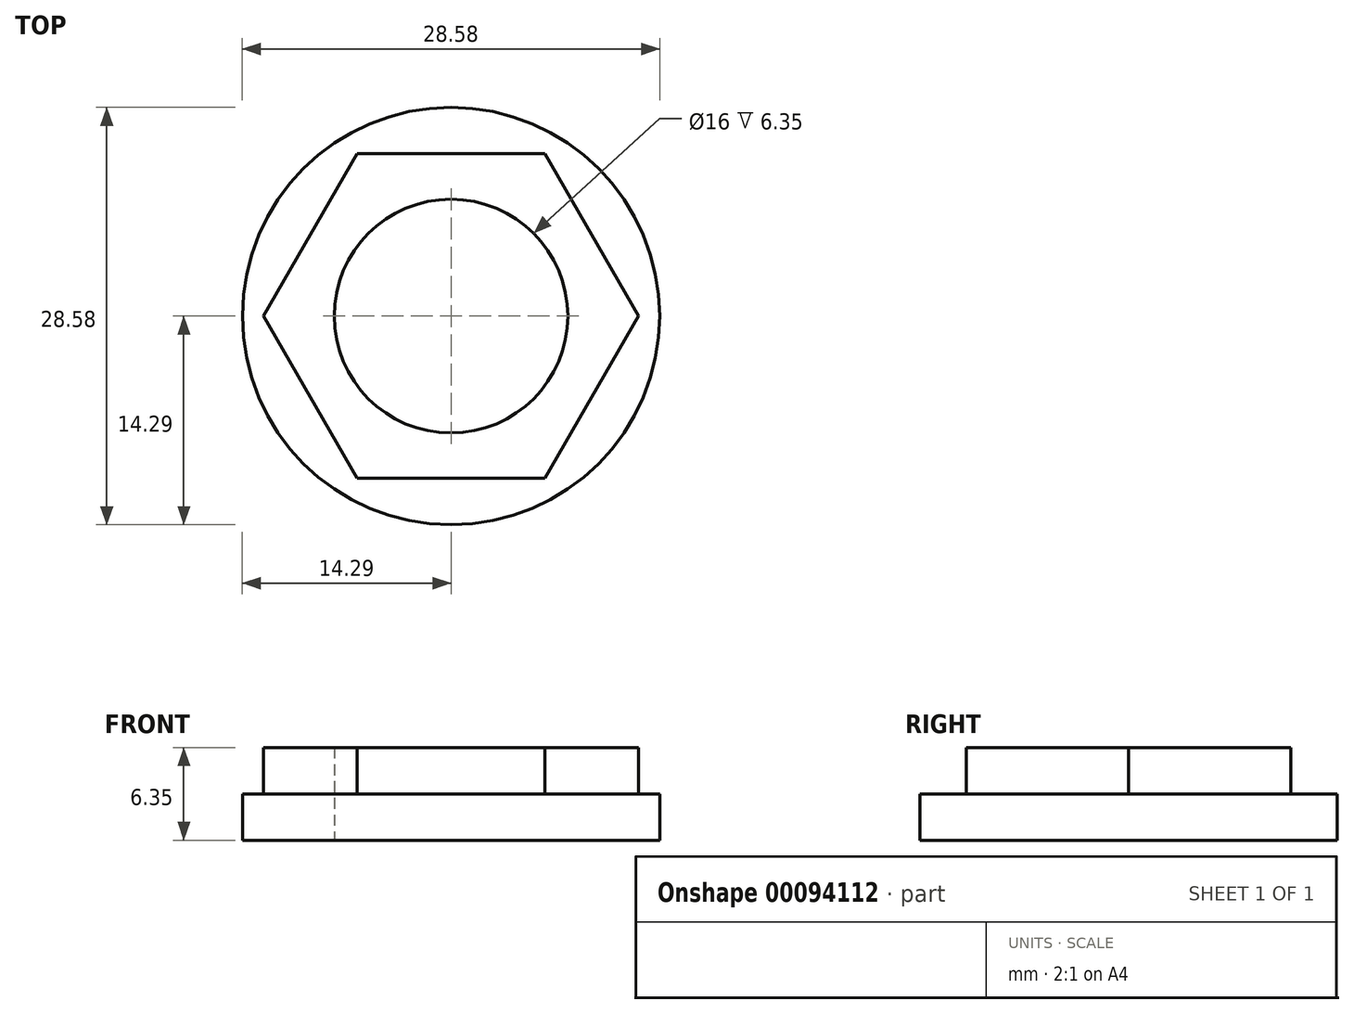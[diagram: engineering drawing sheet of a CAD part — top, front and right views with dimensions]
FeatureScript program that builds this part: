
annotation { "Feature Type Name" : "Feature", "Feature Type Description" : "" }
export const myFeature = defineFeature(function(context is Context, id is Id, definition is map)
    precondition{}
    {
        {
            var Q0;
            Q0=qCreatedBy(makeId("Top.planeOp"),FACE);
            var sketch = newSketch(context, id + "F0", { "sketchPlane" : qUnion([Q0])});
            skCircle(sketch, "E0", {"center": v(0, 0) * mm, "radius": 14.29 * mm});
            skSolve(sketch);
        }
        {
            var Q0;
            Q0=makeQuery(id+"F0.imprint","IMPRINT",FACE,{"disambiguationData":[TD([[makeQuery(id+"F0.imprint","IMPRINT",EDGE,{"derivedFrom":sQuery(id+"F0.wireOp",EDGE,"E0")}),1.0]])]});
            extrude(context, id + "F1", {"entities" : qUnion([Q0]), "depth" : 3.17 * mm});
        }
        {
            var Q0;
            Q0=makeQuery(id+"F1.opExtrude","CAP_FACE",FACE,{"disambiguationData":[OSD([sQuery(id+"F0.wireOp",EDGE,"E0")])],"isStart":false});
            var sketch = newSketch(context, id + "F2", { "sketchPlane" : qUnion([Q0])});
            skCircle(sketch, "E1.0", {"center": v(0, 0) * mm, "radius": 14.29 * mm});
            skCircle(sketch, "E2.cCircle", {"center": v(0, 0) * mm, "radius": 11.11 * mm, "construction": true});
            skLineSegment(sketch, "E2.0", {"start": v(-6.42, 11.11) * mm, "end": v(6.42, 11.11) * mm});
            skLineSegment(sketch, "E2.1", {"start": v(6.42, 11.11) * mm, "end": v(12.83, 0) * mm});
            skLineSegment(sketch, "E2.2", {"start": v(12.83, 0) * mm, "end": v(6.42, -11.11) * mm});
            skLineSegment(sketch, "E2.3", {"start": v(6.42, -11.11) * mm, "end": v(-6.42, -11.11) * mm});
            skLineSegment(sketch, "E2.4", {"start": v(-6.42, -11.11) * mm, "end": v(-12.83, 0) * mm});
            skLineSegment(sketch, "E2.5", {"start": v(-12.83, 0) * mm, "end": v(-6.42, 11.11) * mm});
            skPoint(sketch, "E2.0.midPoint", {"position": v(0, 11.11) * mm});
            skSolve(sketch);
        }
        {
            var Q0;
            Q0=makeQuery(id+"F2.imprint","IMPRINT",FACE,{"disambiguationData":[TD([[makeQuery(id+"F2.imprint","IMPRINT",EDGE,{"derivedFrom":sQuery(id+"F2.wireOp",EDGE,"E2.0")}),-1.0]])]});
            extrude(context, id + "F3", {"entities" : qUnion([Q0]), "operationType" : NewBodyOperationType.ADD, "depth" : 3.17 * mm});
        }
        {
            var Q0;
            Q0=makeQuery(id+"F1.opExtrude","CAP_FACE",FACE,{"disambiguationData":[OSD([sQuery(id+"F0.wireOp",EDGE,"E0")])],"isStart":true});
            var sketch = newSketch(context, id + "F4", { "sketchPlane" : qUnion([Q0])});
            skCircle(sketch, "E3.0", {"center": v(0, 0) * mm, "radius": 14.29 * mm});
            skCircle(sketch, "E4", {"center": v(0, 0) * mm, "radius": 8 * mm});
            skSolve(sketch);
        }
        {
            var Q0;
            Q0=makeQuery(id+"F4.imprint","IMPRINT",FACE,{"disambiguationData":[TD([[makeQuery(id+"F4.imprint","IMPRINT",EDGE,{"derivedFrom":sQuery(id+"F4.wireOp",EDGE,"E4")}),1.0]])]});
            extrude(context, id + "F5", {"entities" : qUnion([Q0]), "operationType" : NewBodyOperationType.REMOVE, "oppositeDirection" : true, "depth" : 25.4 * mm});
        }
    });
